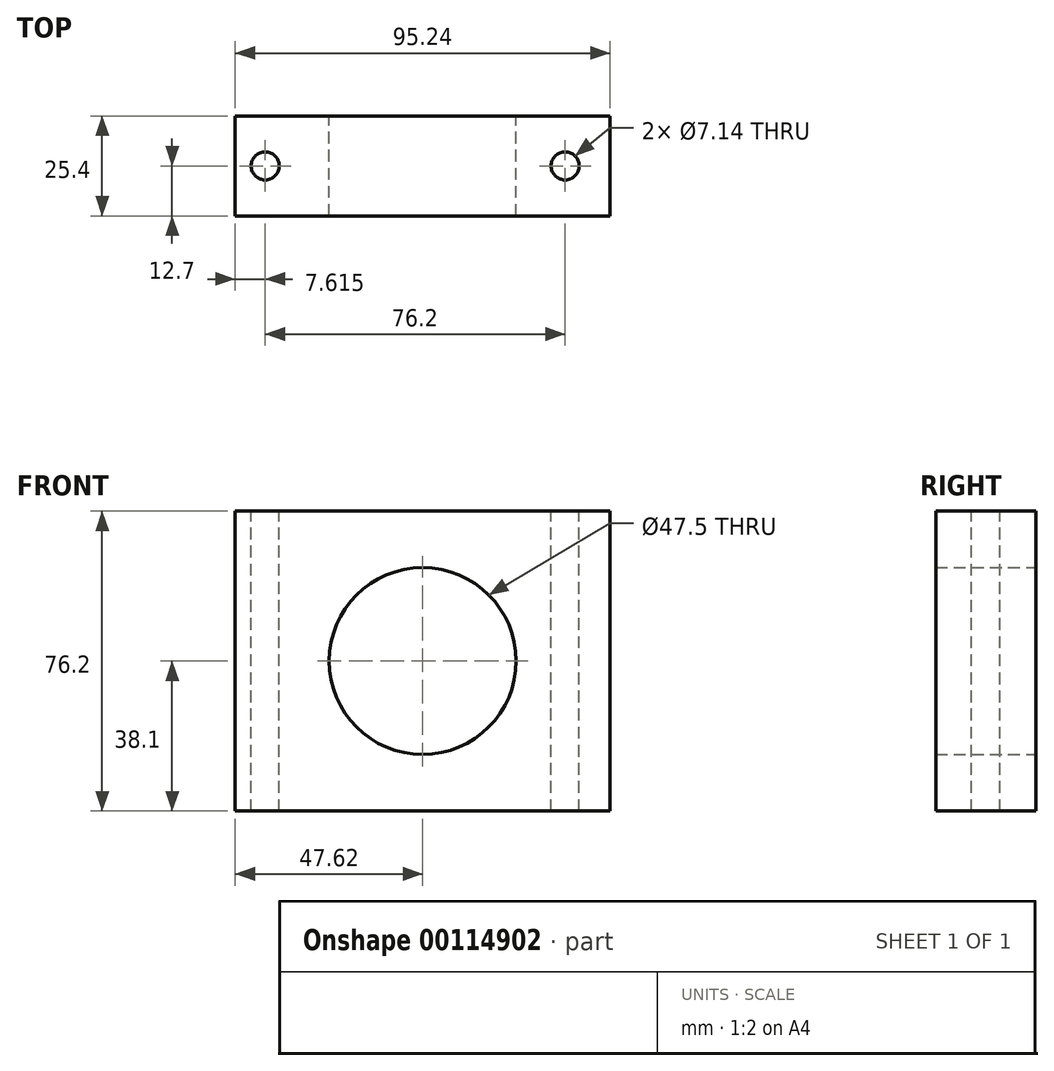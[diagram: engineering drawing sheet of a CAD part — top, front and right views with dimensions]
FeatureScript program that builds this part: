
annotation { "Feature Type Name" : "Feature", "Feature Type Description" : "" }
export const myFeature = defineFeature(function(context is Context, id is Id, definition is map)
    precondition{}
    {
        {
            var Q0;
            Q0=qCreatedBy(makeId("Front.planeOp"),FACE);
            var sketch = newSketch(context, id + "F0", { "sketchPlane" : qUnion([Q0])});
            skLineSegment(sketch, "E0.bottom", {"start": v(47.63, -38.1) * mm, "end": v(-47.63, -38.1) * mm});
            skLineSegment(sketch, "E0.top", {"start": v(47.63, 38.1) * mm, "end": v(-47.63, 38.1) * mm});
            skLineSegment(sketch, "E0.left", {"start": v(47.63, -38.1) * mm, "end": v(47.63, 38.1) * mm});
            skLineSegment(sketch, "E0.right", {"start": v(-47.63, -38.1) * mm, "end": v(-47.63, 38.1) * mm});
            skPoint(sketch, "E0.middle", {"position": v(0, 0) * mm});
            skLineSegment(sketch, "E1", {"start": v(-76.05, 0) * mm, "end": v(77.14, 0) * mm, "construction": true});
            skPoint(sketch, "E1.endSnap0", {"position": v(47.63, 0) * mm});
            skLineSegment(sketch, "E2", {"start": v(0, 76.77) * mm, "end": v(0, -76.43) * mm, "construction": true});
            skCircle(sketch, "E3", {"center": v(0, 0) * mm, "radius": 23.75 * mm});
            skSolve(sketch);
        }
        {
            var Q0;
            Q0=qSketchRegion(id+"F0",true);
            extrude(context, id + "F1", {"entities" : qUnion([Q0]), "depth" : 25.4 * mm});
        }
        {
            var Q0;
            Q0=makeQuery(id+"F1.opExtrude","SWEPT_FACE",FACE,{"disambiguationData":[OSD([sQuery(id+"F0.wireOp",EDGE,"E0.top")])]});
            var sketch = newSketch(context, id + "F2", { "sketchPlane" : qUnion([Q0])});
            skLineSegment(sketch, "E4", {"start": v(0, 0) * mm, "end": v(0, -25.4) * mm, "construction": true});
            skLineSegment(sketch, "E5", {"start": v(-47.63, -12.7) * mm, "end": v(47.63, -12.7) * mm, "construction": true});
            skPoint(sketch, "E6", {"position": v(-40, -12.7) * mm});
            skPoint(sketch, "E7", {"position": v(36.2, -12.7) * mm});
            skPoint(sketch, "E8", {"position": v(47.63, 0) * mm});
            skCircle(sketch, "E9", {"center": v(-40, -12.7) * mm, "radius": 3.57 * mm});
            skCircle(sketch, "E10", {"center": v(36.2, -12.7) * mm, "radius": 3.57 * mm});
            skSolve(sketch);
        }
        {
            var Q0;
            Q0=qSketchRegion(id+"F2",true);
            extrude(context, id + "F3", {"entities" : qUnion([Q0]), "operationType" : NewBodyOperationType.REMOVE, "endBound" : BoundingType.THROUGH_ALL, "oppositeDirection" : true, "depth" : 25.4 * mm});
        }
    });
